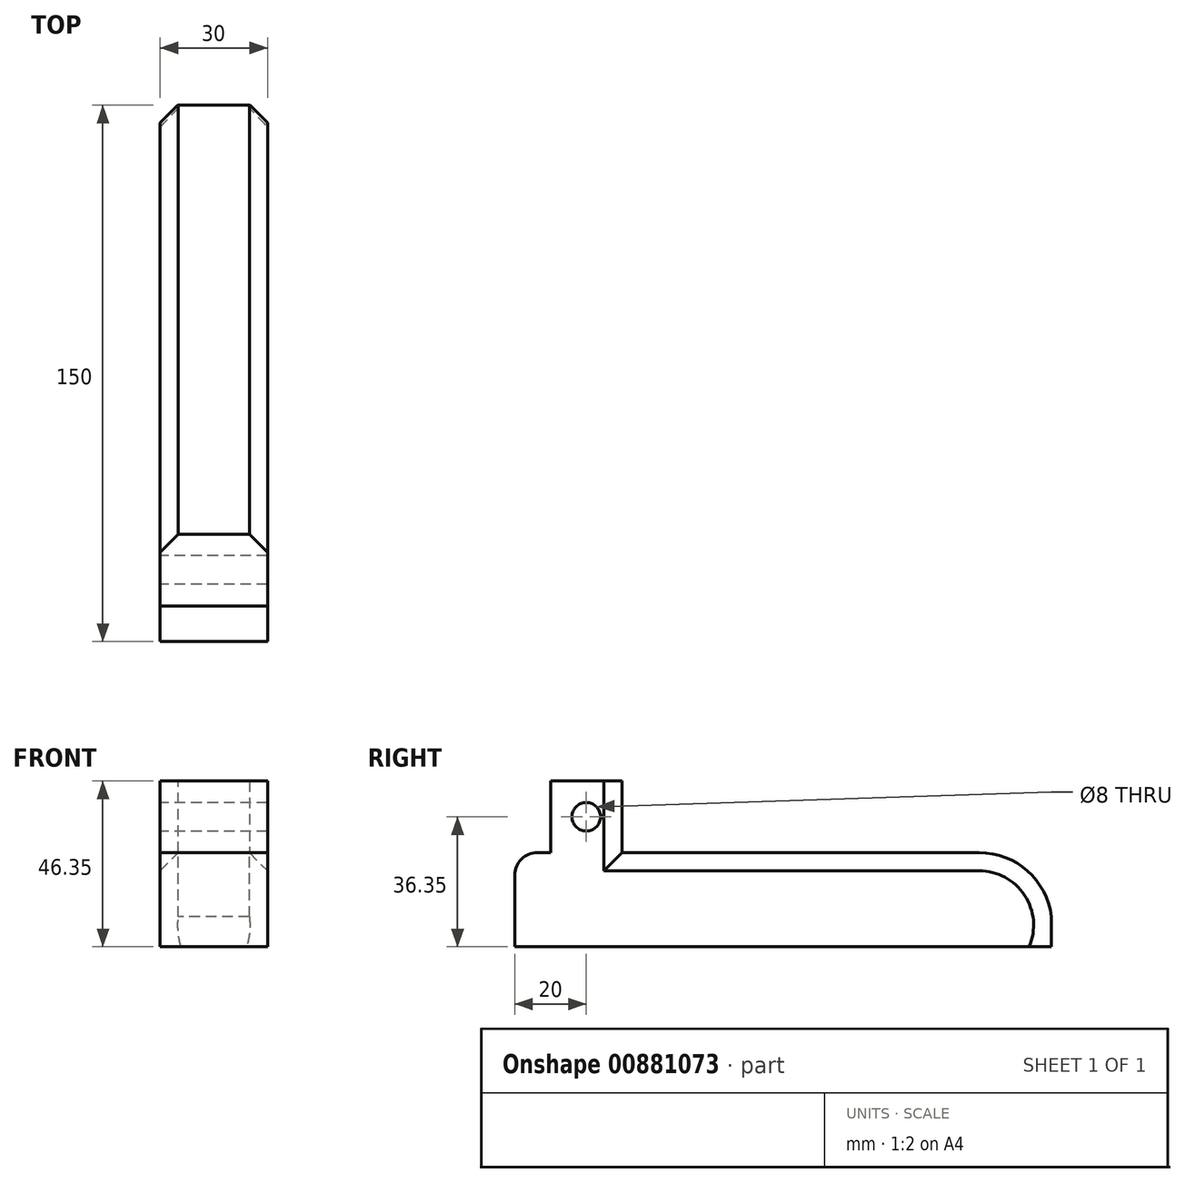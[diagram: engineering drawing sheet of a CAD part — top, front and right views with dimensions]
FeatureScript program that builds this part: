
annotation { "Feature Type Name" : "Feature", "Feature Type Description" : "" }
export const myFeature = defineFeature(function(context is Context, id is Id, definition is map)
    precondition{}
    {
        {
            var Q0;
            Q0=qCreatedBy(makeId("Right.planeOp"),FACE);
            var sketch = newSketch(context, id + "F0", { "sketchPlane" : qUnion([Q0])});
            skLineSegment(sketch, "E0.bottom", {"start": v(0, 0) * mm, "end": v(150, 0) * mm});
            skLineSegment(sketch, "E0.top", {"start": v(6.35, 26.35) * mm, "end": v(10, 26.35) * mm});
            skLineSegment(sketch, "E0.left", {"start": v(0, 0) * mm, "end": v(0, 20) * mm});
            skLineSegment(sketch, "E0.right", {"start": v(150, 0) * mm, "end": v(150, 8.4) * mm});
            skLineSegment(sketch, "E1", {"start": v(10, 26.35) * mm, "end": v(10, 46.35) * mm});
            skLineSegment(sketch, "E2", {"start": v(10, 46.35) * mm, "end": v(30, 46.35) * mm});
            skLineSegment(sketch, "E3", {"start": v(30, 46.35) * mm, "end": v(30, 26.35) * mm});
            skLineSegment(sketch, "E4.trimOffspring", {"start": v(30, 26.35) * mm, "end": v(129.82, 26.35) * mm});
            skPoint(sketch, "E5.visualSharp", {"position": v(0, 26.35) * mm});
            skArc(sketch, "E5.filletArc", {"start": v(6.35, 26.35) * mm, "mid": v(1.86, 24.5) * mm, "end": v(0, 20) * mm});
            skCircle(sketch, "E6", {"center": v(20, 36.35) * mm, "radius": 4 * mm});
            skPoint(sketch, "E7.visualSharp", {"position": v(132.14, 26.35) * mm});
            skPoint(sketch, "E8.visualSharp", {"position": v(150, 11.35) * mm});
            skArc(sketch, "E9", {"start": v(129.82, 26.35) * mm, "mid": v(143.33, 21.2) * mm, "end": v(150, 8.4) * mm});
            skSolve(sketch);
        }
        {
            var Q0;
            Q0 = qSketchRegion(id + "F0", true);
            extrude(context, id + "F1", {"entities" : qUnion([Q0]), "depth" : 30 * mm, "offsetDistance" : 25.4 * mm});
        }
        {
            var Q0;
            Q0=makeQuery(id+"F1.opExtrude","CAP_EDGE",EDGE,{"disambiguationData":[OSD([sQuery(id+"F0.wireOp",EDGE,"E4.trimOffspring")])],"isStart":false});
            var Q1;
            Q1=makeQuery(id+"F1.opExtrude","CAP_EDGE",EDGE,{"disambiguationData":[OSD([sQuery(id+"F0.wireOp",EDGE,"E3")])],"isStart":false});
            var Q2;
            Q2=makeQuery(id+"F1.opExtrude","CAP_EDGE",EDGE,{"disambiguationData":[OSD([sQuery(id+"F0.wireOp",EDGE,"E3")])],"isStart":true});
            var Q3;
            Q3=makeQuery(id+"F1.opExtrude","CAP_EDGE",EDGE,{"disambiguationData":[OSD([sQuery(id+"F0.wireOp",EDGE,"E4.trimOffspring")])],"isStart":true});
            chamfer(context, id + "F2", {"entities" : qUnion([Q0, Q1, Q2, Q3]), "width" : 5.08 * mm, "tangentPropagation" : true});
        }
    });
